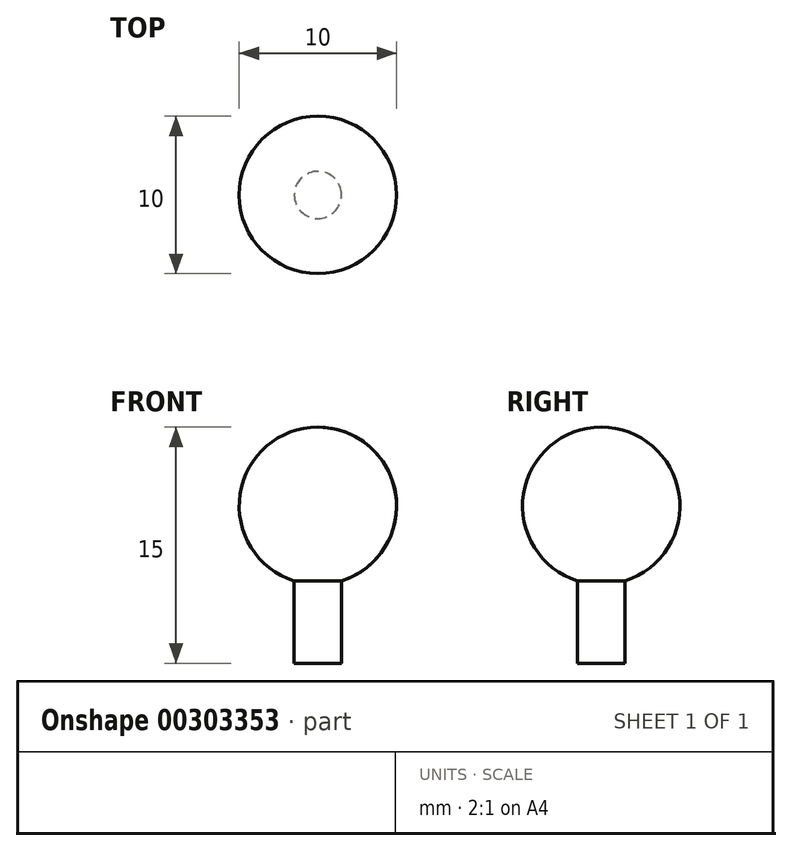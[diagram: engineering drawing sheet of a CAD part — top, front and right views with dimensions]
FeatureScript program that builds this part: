
annotation { "Feature Type Name" : "Feature", "Feature Type Description" : "" }
export const myFeature = defineFeature(function(context is Context, id is Id, definition is map)
    precondition{}
    {
        {
            var Q0;
            Q0=qCreatedBy(makeId("Front.planeOp"),FACE);
            var sketch = newSketch(context, id + "F0", { "sketchPlane" : qUnion([Q0])});
            skLineSegment(sketch, "E0.top", {"start": v(0, -10) * mm, "end": v(1.5, -10) * mm});
            skLineSegment(sketch, "E0.right", {"start": v(1.5, -4.77) * mm, "end": v(1.5, -10) * mm});
            skPoint(sketch, "E0.middle", {"position": v(0, 0) * mm});
            skArc(sketch, "E1", {"start": v(1.5, -4.77) * mm, "mid": v(4.94, 0.76) * mm, "end": v(0, 5) * mm});
            skLineSegment(sketch, "E2", {"start": v(0, 5) * mm, "end": v(0, -10) * mm});
            skSolve(sketch);
        }
        {
            var Q0;
            Q0=makeQuery(id+"F0.imprint","IMPRINT",FACE,{"disambiguationData":[TD([[makeQuery(id+"F0.imprint","IMPRINT",EDGE,{"derivedFrom":sQuery(id+"F0.wireOp",EDGE,"E0.top")}),1.0]])]});
            var Q1;
            Q1=sQuery(id+"F0.wireOp",EDGE,"E2");
            revolve(context, id + "F1", {"entities" : qUnion([Q0]), "axis" : qUnion([Q1]), "revolveType" : RevolveType.FULL});
        }
    });
